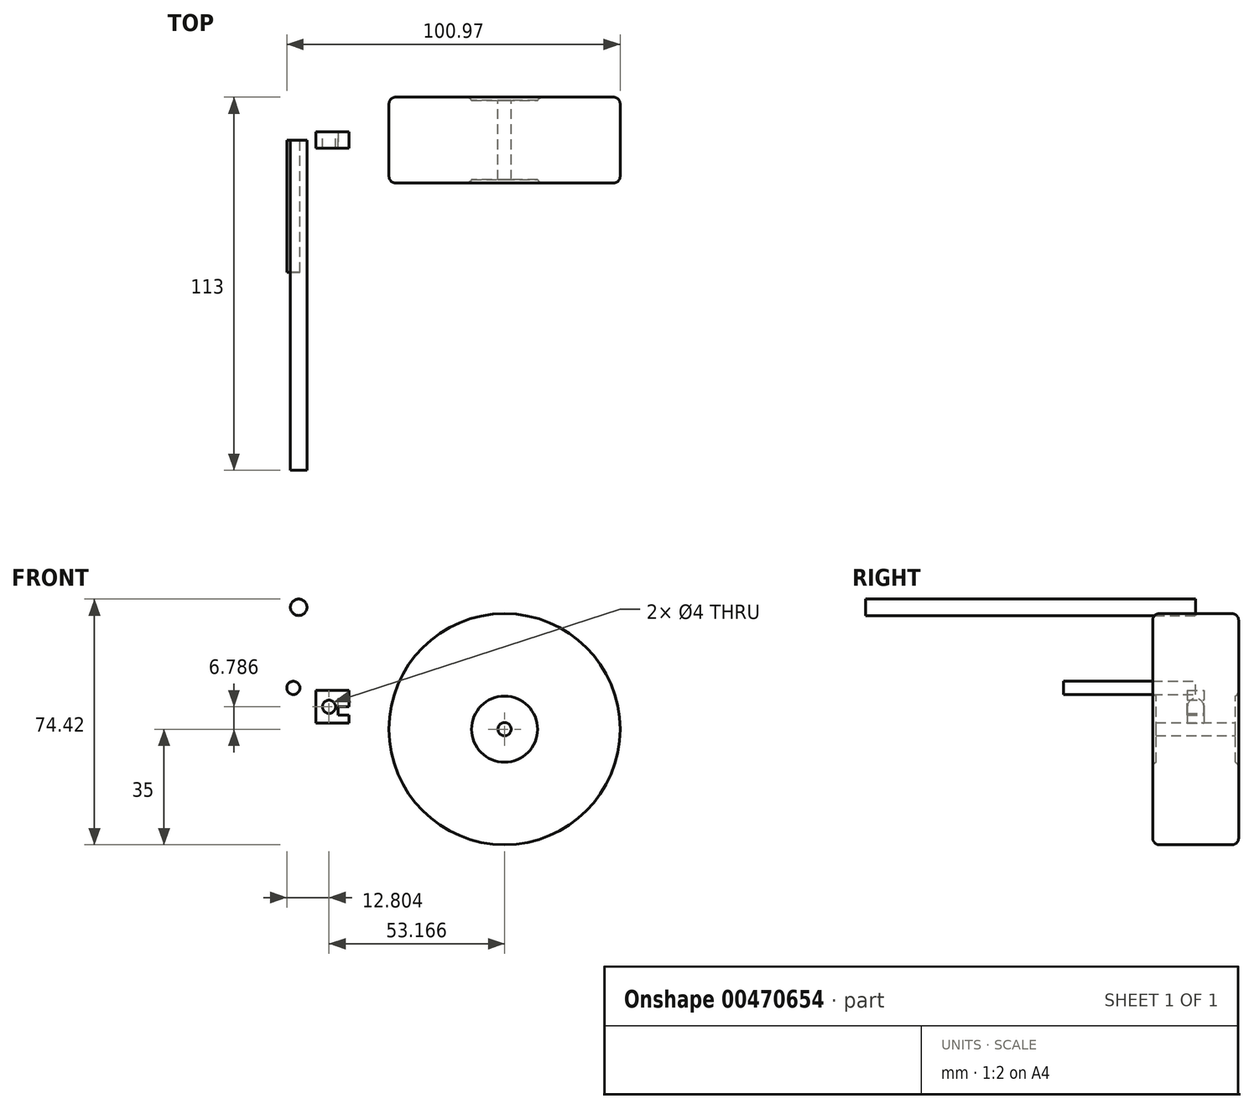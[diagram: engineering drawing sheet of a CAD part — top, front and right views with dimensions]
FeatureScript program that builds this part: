
annotation { "Feature Type Name" : "Feature", "Feature Type Description" : "" }
export const myFeature = defineFeature(function(context is Context, id is Id, definition is map)
    precondition{}
    {
        {
            var Q0;
            Q0=qCreatedBy(makeId("Front.planeOp"),FACE);
            var sketch = newSketch(context, id + "F0", { "sketchPlane" : qUnion([Q0])});
            skCircle(sketch, "E0", {"center": v(0, 0) * mm, "radius": 10 * mm});
            skCircle(sketch, "E1", {"center": v(0, 0) * mm, "radius": 2 * mm});
            skCircle(sketch, "E2", {"center": v(0, 0) * mm, "radius": 35 * mm});
            skSolve(sketch);
        }
        {
            var Q0;
            Q0=makeQuery(id+"F0.imprint","IMPRINT",FACE,{"disambiguationData":[TD([[makeQuery(id+"F0.imprint","IMPRINT",EDGE,{"derivedFrom":sQuery(id+"F0.wireOp",EDGE,"E0")}),1.0]])]});
            extrude(context, id + "F1", {"entities" : qUnion([Q0]), "endBound" : BoundingType.SYMMETRIC, "depth" : 24 * mm});
        }
        {
            var Q0;
            Q0=makeQuery(id+"F0.imprint","IMPRINT",FACE,{"disambiguationData":[TD([[makeQuery(id+"F0.imprint","IMPRINT",EDGE,{"derivedFrom":sQuery(id+"F0.wireOp",EDGE,"E0")}),-1.0]])]});
            extrude(context, id + "F2", {"entities" : qUnion([Q0]), "operationType" : NewBodyOperationType.ADD, "endBound" : BoundingType.SYMMETRIC, "depth" : 26 * mm});
        }
        {
            var Q0;
            Q0=makeQuery(id+"F2.opExtrude","CAP_EDGE",EDGE,{"disambiguationData":[OSD([sQuery(id+"F0.wireOp",EDGE,"E0")])],"isStart":true});
            var Q1;
            Q1=makeQuery(id+"F2.opExtrude","CAP_EDGE",EDGE,{"disambiguationData":[OSD([sQuery(id+"F0.wireOp",EDGE,"E0")])],"isStart":false});
            var Q2;
            Q2=makeQuery(id+"F2.opExtrude","CAP_EDGE",EDGE,{"disambiguationData":[OSD([sQuery(id+"F0.wireOp",EDGE,"E2")])],"isStart":false});
            var Q3;
            Q3=makeQuery(id+"F2.opExtrude","CAP_EDGE",EDGE,{"disambiguationData":[OSD([sQuery(id+"F0.wireOp",EDGE,"E2")])],"isStart":true});
            fillet(context, id + "F3", {"entities" : qUnion([Q0, Q1, Q2, Q3]), "radius" : 2 * mm, "tangentPropagation" : true, "allowEdgeOverflow" : false});
        }
        {
            var Q0;
            Q0=qCreatedBy(makeId("Front.planeOp"),FACE);
            var sketch = newSketch(context, id + "F4", { "sketchPlane" : qUnion([Q0])});
            skCircle(sketch, "E3", {"center": v(-62.34, 36.92) * mm, "radius": 2.5 * mm});
            skCircle(sketch, "E4", {"center": v(-63.97, 12.5) * mm, "radius": 2 * mm});
            skLineSegment(sketch, "E5.bottom", {"start": v(-47.17, 11.79) * mm, "end": v(-57.17, 11.79) * mm});
            skLineSegment(sketch, "E5.top", {"start": v(-47.17, 1.79) * mm, "end": v(-57.17, 1.79) * mm});
            skLineSegment(sketch, "E5.left", {"start": v(-47.17, 11.79) * mm, "end": v(-47.17, 1.79) * mm});
            skLineSegment(sketch, "E5.right", {"start": v(-57.17, 11.79) * mm, "end": v(-57.17, 1.79) * mm});
            skPoint(sketch, "E5.middle", {"position": v(-52.17, 6.79) * mm});
            skLineSegment(sketch, "E6", {"start": v(-57.17, 3.29) * mm, "end": v(-47.17, 3.29) * mm});
            skLineSegment(sketch, "E7", {"start": v(-47.17, 10.29) * mm, "end": v(-57.17, 10.29) * mm});
            skCircle(sketch, "E8", {"center": v(-53.17, 6.79) * mm, "radius": 2 * mm});
            skLineSegment(sketch, "E9", {"start": v(-50.47, 3.29) * mm, "end": v(-50.47, 10.29) * mm});
            skLineSegment(sketch, "E10", {"start": v(-50.47, 6.79) * mm, "end": v(-47.17, 6.79) * mm});
            skLineSegment(sketch, "E11", {"start": v(-47.17, 9.29) * mm, "end": v(-50.47, 9.29) * mm});
            skLineSegment(sketch, "E12", {"start": v(-47.17, 4.29) * mm, "end": v(-50.47, 4.29) * mm});
            skSolve(sketch);
        }
        {
            var Q0;
            Q0=makeQuery(id+"F4.imprint","IMPRINT",FACE,{"disambiguationData":[TD([[makeQuery(id+"F4.imprint","IMPRINT",EDGE,{"derivedFrom":sQuery(id+"F4.wireOp",EDGE,"E3")}),1.0]])]});
            extrude(context, id + "F5", {"entities" : qUnion([Q0]), "depth" : 100 * mm});
        }
        {
            var Q0;
            Q0=makeQuery(id+"F4.imprint","IMPRINT",FACE,{"disambiguationData":[TD([[makeQuery(id+"F4.imprint","IMPRINT",EDGE,{"derivedFrom":sQuery(id+"F4.wireOp",EDGE,"E4")}),1.0]])]});
            extrude(context, id + "F6", {"entities" : qUnion([Q0]), "depth" : 40 * mm});
        }
        {
            var Q0;
            {var subQ4=sQuery(id+"F4.wireOp",EDGE,"E5.bottom");Q0=makeQuery(id+"F4.imprint","IMPRINT",FACE,{"disambiguationData":[TD([[makeQuery(id+"F4.imprint","IMPRINT",EDGE,{"derivedFrom":subQ4}),1.0]])]});}
            var Q1;
            Q1=makeQuery(id+"F4.imprint","IMPRINT",FACE,{"disambiguationData":[TD([[makeQuery(id+"F4.imprint","IMPRINT",EDGE,{"derivedFrom":sQuery(id+"F4.wireOp",EDGE,"E8")}),-1.0]])]});
            var Q2;
            {var subQ4=sQuery(id+"F4.wireOp",EDGE,"E5.top");Q2=makeQuery(id+"F4.imprint","IMPRINT",FACE,{"disambiguationData":[TD([[makeQuery(id+"F4.imprint","IMPRINT",EDGE,{"derivedFrom":subQ4}),-1.0]])]});}
            var Q3;
            {var subQ3=sQuery(id+"F4.wireOp",EDGE,"E11");Q3=makeQuery(id+"F4.imprint","IMPRINT",FACE,{"disambiguationData":[TD([[makeQuery(id+"F4.imprint","IMPRINT",EDGE,{"derivedFrom":subQ3}),-1.0]])]});}
            var Q4;
            {var subQ0=sQuery(id+"F4.wireOp",EDGE,"E10");Q4=makeQuery(id+"F4.imprint","IMPRINT",FACE,{"disambiguationData":[TD([[makeQuery(id+"F4.imprint","IMPRINT",EDGE,{"derivedFrom":subQ0}),1.0]])]});}
            var Q5;
            {var subQ3=sQuery(id+"F4.wireOp",EDGE,"E12");Q5=makeQuery(id+"F4.imprint","IMPRINT",FACE,{"disambiguationData":[TD([[makeQuery(id+"F4.imprint","IMPRINT",EDGE,{"derivedFrom":subQ3}),1.0]])]});}
            extrude(context, id + "F7", {"entities" : qUnion([Q0, Q1, Q2, Q3, Q4, Q5]), "endBound" : BoundingType.SYMMETRIC, "depth" : 5 * mm});
        }
        {
            var Q0;
            {var subQ0=sQuery(id+"F4.wireOp",EDGE,"E10");Q0=makeQuery(id+"F4.imprint","IMPRINT",FACE,{"disambiguationData":[TD([[makeQuery(id+"F4.imprint","IMPRINT",EDGE,{"derivedFrom":subQ0}),-1.0]])]});}
            var Q1;
            Q1=sQuery(id+"F4.wireOp",EDGE,"E10");
            revolve(context, id + "F8", {"operationType" : NewBodyOperationType.REMOVE, "entities" : qUnion([Q0]), "axis" : qUnion([Q1]), "revolveType" : RevolveType.FULL, "oppositeDirection" : true});
        }
    });
